# Revit family: bytec_EI60
name_source: partatom
category: Обобщенные модели
revit_build: Autodesk Revit 2016 (Build: 20150714_1515(x64)
units: mm (PartAtom-declared; Revit-internal decimal feet)

## family parameters
Всегда вертикально = Да
Может служить основой для арматурных стержней = Нет
Общий = Нет
Основа = Стена
При загрузке вырезать с полостями = Нет
Размер круглого соединителя = Использовать диаметр
Тип детали = Нормальный
Точка расчета площади = Нет

## types (1)
- Противопожарная штора ШОЗ EI60
    ADSK_Единица измерения = шт.
    FL_Таблица1 = СеткаКоробов1
    URL = http://fireproof.bikoms.ru
    Высота лаза = 2000 мм
    Высота люка = 300 мм
    Выступ = 1 мм
    Глубина направляющих = 45 мм
    Изготовитель = ООО 'БиКомс Холдинг'
    Ключевая пометка = ﻿﻿ ​ ​​​​​​   ﻿ ​   ﻿       ​ ﻿ ​ ​ ﻿ ​   ﻿       ​ ﻿   ﻿     ﻿   ​       ﻿  ﻿ ﻿   ﻿ ﻿   ﻿        ​​ ​        ​ ﻿   ​ ﻿ ​                ﻿                ​  ﻿        ﻿﻿
    Код по классификатору = ﻿﻿ ​ ​​​​​​   ﻿ ​   ﻿       ​ ﻿ ​ ​ ﻿ ​   ﻿       ​ ﻿   ﻿     ﻿   ​       ﻿  ﻿ ﻿   ﻿ ﻿   ﻿        ​​ ​        ​ ﻿   ​ ﻿ ​                ﻿                ​  ﻿        ﻿﻿
    Комментарии к типоразмеру = ﻿﻿ ​ ​​​​​​   ﻿ ​   ﻿       ​ ﻿ ​ ​ ﻿ ​   ﻿       ​ ﻿   ﻿     ﻿   ​       ﻿  ﻿ ﻿   ﻿ ﻿   ﻿        ​​ ​        ​ ﻿   ​ ﻿ ​                ﻿                ​  ﻿        ﻿﻿
    Материал короба = Сталь х/к 0,8ПС  1.5мм
    Материал направляющих = Сталь х/к 0,8ПС  1.5мм
    Материал полотна = Полотно EI 60
    Описание = ﻿﻿ ​ ​​​​​​   ﻿ ​   ﻿       ​ ﻿ ​ ​ ﻿ ​   ﻿       ​ ﻿   ﻿     ﻿   ​       ﻿  ﻿ ﻿   ﻿ ﻿   ﻿        ​​ ​        ​ ﻿   ​ ﻿ ​                ﻿                ​  ﻿        ﻿﻿
    Отстаяние лючка от центра = 400 мм
    Ток1 = 10 А
    Толщина направляющих = 90 мм
    Толщина полотна = 8 мм
    Ширина лаза = 50 мм
    Ширина люка = 150 мм
    Электросеть = 220 В

## geometry (parser evidence)
native form markers: Blend x2
no freeform markers — native parametric forms only
